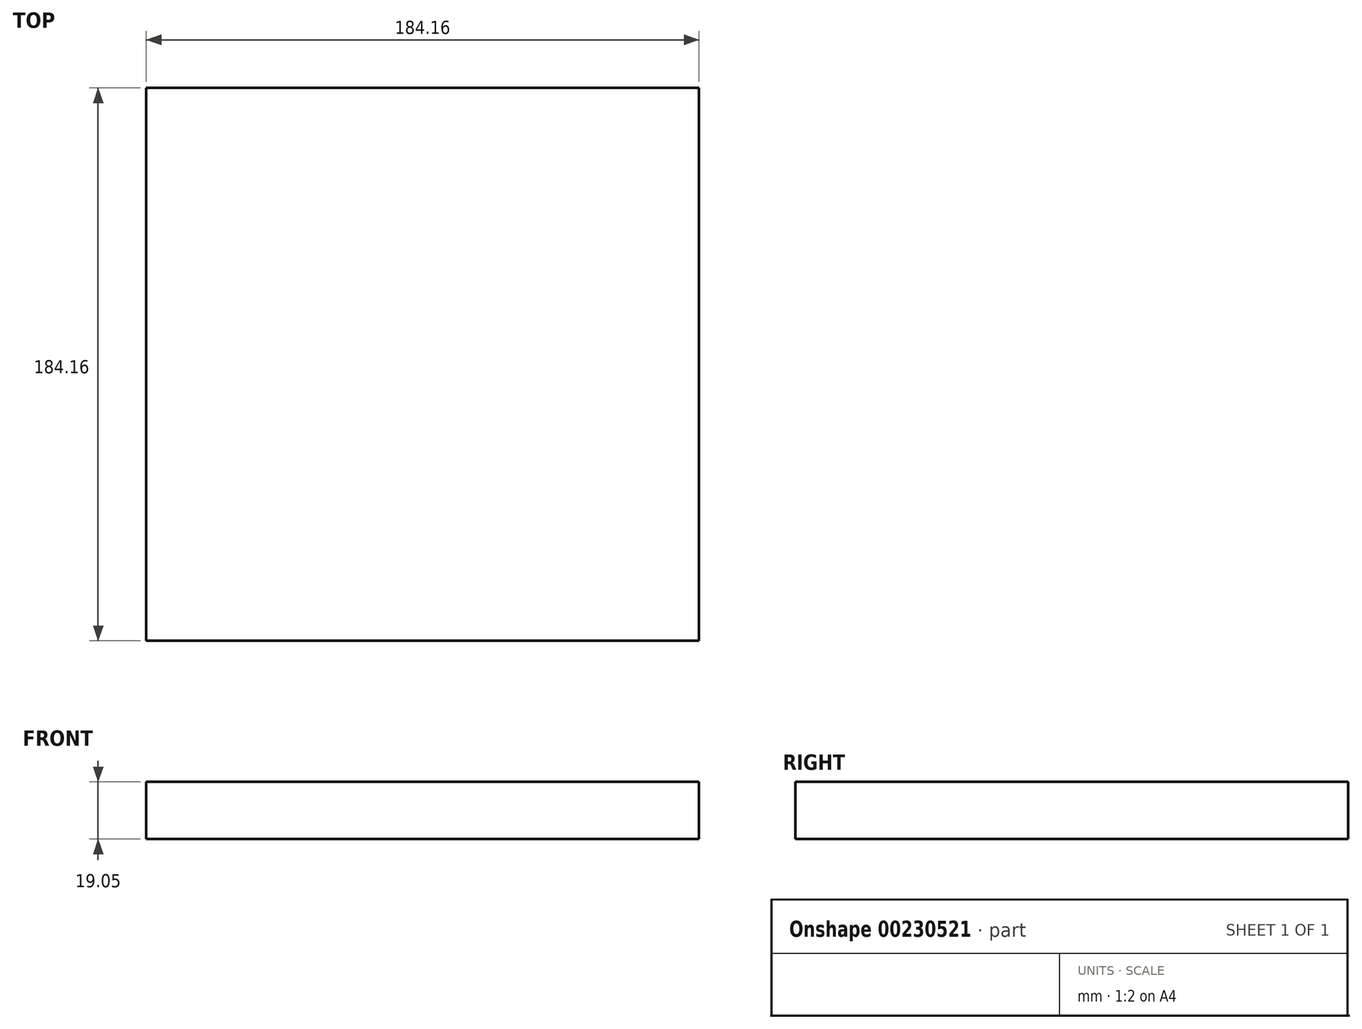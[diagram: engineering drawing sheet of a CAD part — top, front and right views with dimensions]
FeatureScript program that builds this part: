
annotation { "Feature Type Name" : "Feature", "Feature Type Description" : "" }
export const myFeature = defineFeature(function(context is Context, id is Id, definition is map)
    precondition{}
    {
        {
            var Q0;
            Q0=qCreatedBy(makeId("Top.planeOp"),FACE);
            var sketch = newSketch(context, id + "F0", { "sketchPlane" : qUnion([Q0])});
            skLineSegment(sketch, "E0.bottom", {"start": v(-92.08, -92.08) * mm, "end": v(92.07, -92.08) * mm});
            skLineSegment(sketch, "E0.top", {"start": v(-92.08, 92.08) * mm, "end": v(92.08, 92.08) * mm});
            skLineSegment(sketch, "E0.left", {"start": v(-92.08, -92.08) * mm, "end": v(-92.08, 92.08) * mm});
            skLineSegment(sketch, "E0.right", {"start": v(92.07, -92.08) * mm, "end": v(92.08, 92.08) * mm});
            skPoint(sketch, "E0.middle", {"position": v(0, 0) * mm});
            skSolve(sketch);
        }
        {
            var Q0;
            Q0 = qSketchRegion(id + "F0", true);
            extrude(context, id + "F1", {"entities" : qUnion([Q0]), "depth" : 19.05 * mm});
        }
    });
